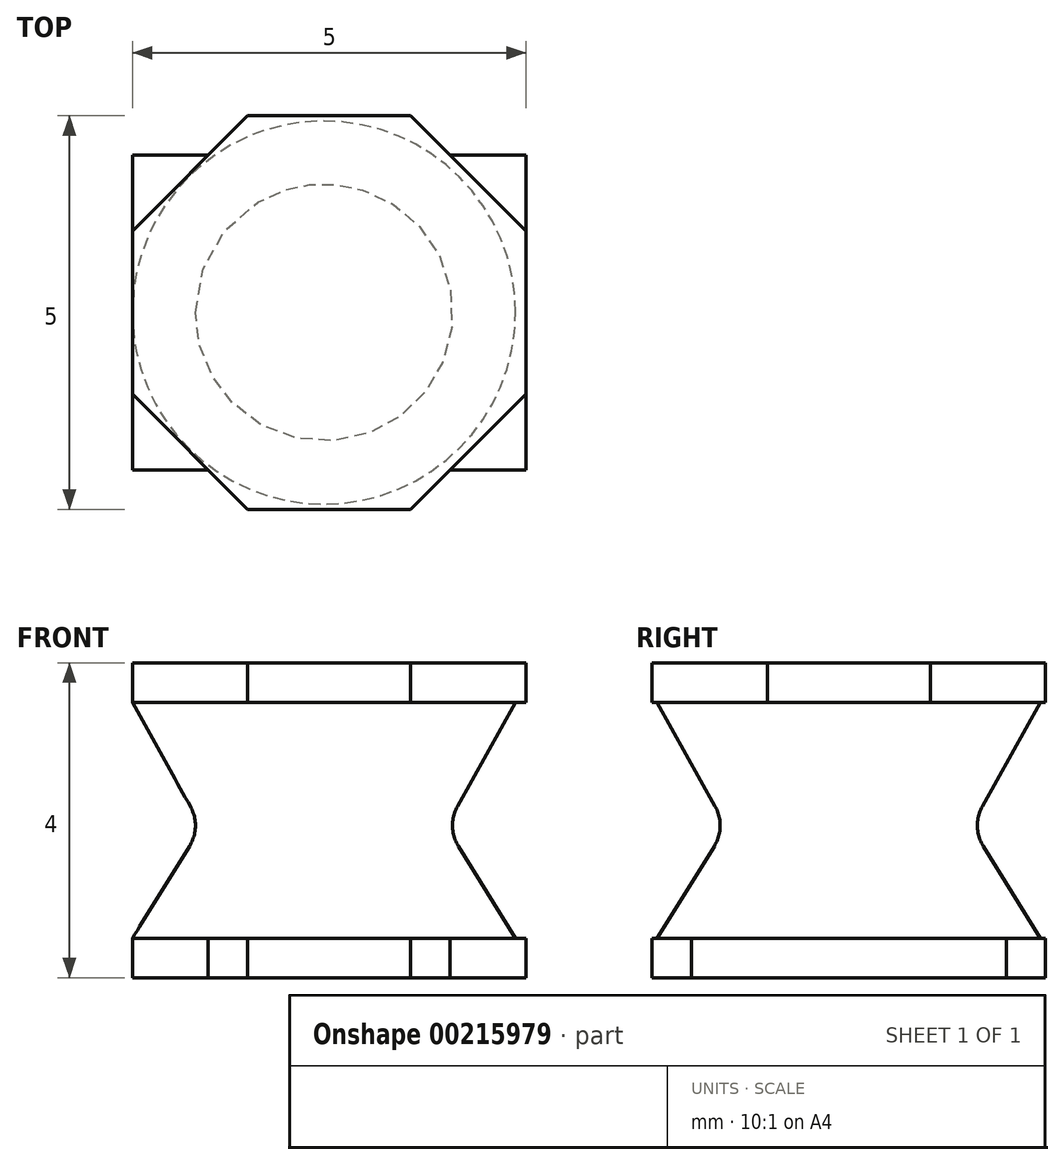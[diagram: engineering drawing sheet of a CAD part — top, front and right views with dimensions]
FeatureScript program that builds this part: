
annotation { "Feature Type Name" : "Feature", "Feature Type Description" : "" }
export const myFeature = defineFeature(function(context is Context, id is Id, definition is map)
    precondition{}
    {
        {
            var Q0;
            Q0=qCreatedBy(makeId("Top.planeOp"),FACE);
            var sketch = newSketch(context, id + "F0", { "sketchPlane" : qUnion([Q0])});
            skPoint(sketch, "E0.middle", {"position": v(0, 0) * mm});
            skLineSegment(sketch, "E1.bottom", {"start": v(-2.5, 2) * mm, "end": v(-1.25, 2) * mm});
            skLineSegment(sketch, "E1.top", {"start": v(-2.5, -2) * mm, "end": v(-1.25, -2) * mm});
            skLineSegment(sketch, "E1.left", {"start": v(-2.5, 2) * mm, "end": v(-2.5, -2) * mm});
            skLineSegment(sketch, "E1.right", {"start": v(-1.25, 2) * mm, "end": v(-1.25, -2) * mm});
            skLineSegment(sketch, "E2.MirrorCS", {"start": v(1.25, 2) * mm, "end": v(1.25, -2) * mm});
            skLineSegment(sketch, "E3.MirrorCS", {"start": v(2.5, 2) * mm, "end": v(2.5, -2) * mm});
            skLineSegment(sketch, "E4.MirrorCS", {"start": v(2.5, -2) * mm, "end": v(1.25, -2) * mm});
            skLineSegment(sketch, "E5.MirrorCS", {"start": v(2.5, 2) * mm, "end": v(1.25, 2) * mm});
            skSolve(sketch);
        }
        {
            var Q0;
            Q0 = qSketchRegion(id + "F0", true);
            extrude(context, id + "F1", {"entities" : qUnion([Q0]), "depth" : .5 * mm, "offsetDistance" : 25 * mm});
        }
        {
            var Q0;
            Q0=qCreatedBy(makeId("Top.planeOp"),FACE);
            cPlane(context, id + "F2", {"entities" : qUnion([Q0]), "cplaneType" : CPlaneType.OFFSET, "offset" : 4 * mm, "width" : 150 * mm, "height" : 150 * mm});
        }
        {
            var Q0;
            Q0=qCreatedBy(id+"F2.planeOp",FACE);
            var sketch = newSketch(context, id + "F3", { "sketchPlane" : qUnion([Q0])});
            skCircle(sketch, "E6.cCircle", {"center": v(0, 0) * mm, "radius": 2.5 * mm, "construction": true});
            skLineSegment(sketch, "E6.0", {"start": v(-1.04, 2.5) * mm, "end": v(1.04, 2.5) * mm});
            skLineSegment(sketch, "E6.1", {"start": v(1.04, 2.5) * mm, "end": v(2.5, 1.04) * mm});
            skLineSegment(sketch, "E6.2", {"start": v(2.5, 1.04) * mm, "end": v(2.5, -1.04) * mm});
            skLineSegment(sketch, "E6.3", {"start": v(2.5, -1.04) * mm, "end": v(1.04, -2.5) * mm});
            skLineSegment(sketch, "E6.4", {"start": v(1.04, -2.5) * mm, "end": v(-1.04, -2.5) * mm});
            skLineSegment(sketch, "E6.5", {"start": v(-1.04, -2.5) * mm, "end": v(-2.5, -1.04) * mm});
            skLineSegment(sketch, "E6.6", {"start": v(-2.5, -1.04) * mm, "end": v(-2.5, 1.04) * mm});
            skLineSegment(sketch, "E6.7", {"start": v(-2.5, 1.04) * mm, "end": v(-1.04, 2.5) * mm});
            skPoint(sketch, "E6.0.midPoint", {"position": v(0, 2.5) * mm});
            skSolve(sketch);
        }
        {
            var Q0;
            Q0 = qSketchRegion(id + "F3", true);
            extrude(context, id + "F4", {"entities" : qUnion([Q0]), "oppositeDirection" : true, "depth" : .5 * mm, "offsetDistance" : 25 * mm});
        }
        {
            var Q0;
            Q0 = qSketchRegion(id + "F3", true);
            extrude(context, id + "F5", {"entities" : qUnion([Q0]), "operationType" : NewBodyOperationType.ADD, "oppositeDirection" : true, "depth" : 4 * mm, "offsetDistance" : 25 * mm, "hasSecondDirection" : true, "secondDirectionOppositeDirection" : true, "secondDirectionDepth" : 3.5 * mm});
        }
        {
            var Q0;
            Q0=qCreatedBy(makeId("Front.planeOp"),FACE);
            var sketch = newSketch(context, id + "F6", { "sketchPlane" : qUnion([Q0])});
            skLineSegment(sketch, "E7.0.1", {"start": v(-2.5, 4) * mm, "end": v(-2.5, 3.5) * mm, "construction": true});
            skLineSegment(sketch, "E7.0.3", {"start": v(-2.5, 3.5) * mm, "end": v(-2.5, 4) * mm});
            skLineSegment(sketch, "E8.0.1", {"start": v(-2.5, 0) * mm, "end": v(-2.5, 0.5) * mm});
            skLineSegment(sketch, "E8.0.3", {"start": v(-2.5, 0.5) * mm, "end": v(-2.5, 0) * mm, "construction": true});
            skLineSegment(sketch, "E9", {"start": v(-2.5, 3.5) * mm, "end": v(-1.76, 2.18) * mm});
            skLineSegment(sketch, "E10", {"start": v(-1.77, 1.67) * mm, "end": v(-2.5, 0.5) * mm});
            skPoint(sketch, "E11.visualSharp", {"position": v(-1.62, 1.92) * mm});
            skArc(sketch, "E11.filletArc", {"start": v(-1.77, 1.67) * mm, "mid": v(-1.7, 1.92) * mm, "end": v(-1.76, 2.18) * mm});
            skLineSegment(sketch, "E12", {"start": v(-0.07, 0) * mm, "end": v(-0.07, 4.83) * mm, "construction": true});
            skLineSegment(sketch, "E13", {"start": v(-2.5, 3.5) * mm, "end": v(-0.07, 3.5) * mm});
            skLineSegment(sketch, "E14", {"start": v(-2.5, 0.5) * mm, "end": v(-0.07, 0.5) * mm});
            skLineSegment(sketch, "E15", {"start": v(-0.07, 0.5) * mm, "end": v(-0.07, 3.5) * mm});
            skSolve(sketch);
        }
        {
            var Q0;
            Q0=makeQuery(id+"F6.imprint","IMPRINT",FACE,{"disambiguationData":[TD([[makeQuery(id+"F6.imprint","IMPRINT",EDGE,{"derivedFrom":sQuery(id+"F6.wireOp",EDGE,"E9")}),1.0]])]});
            var Q1;
            Q1=sQuery(id+"F6.wireOp",EDGE,"E12");
            revolve(context, id + "F7", {"entities" : qUnion([Q0]), "axis" : qUnion([Q1]), "revolveType" : RevolveType.FULL});
        }
    });
